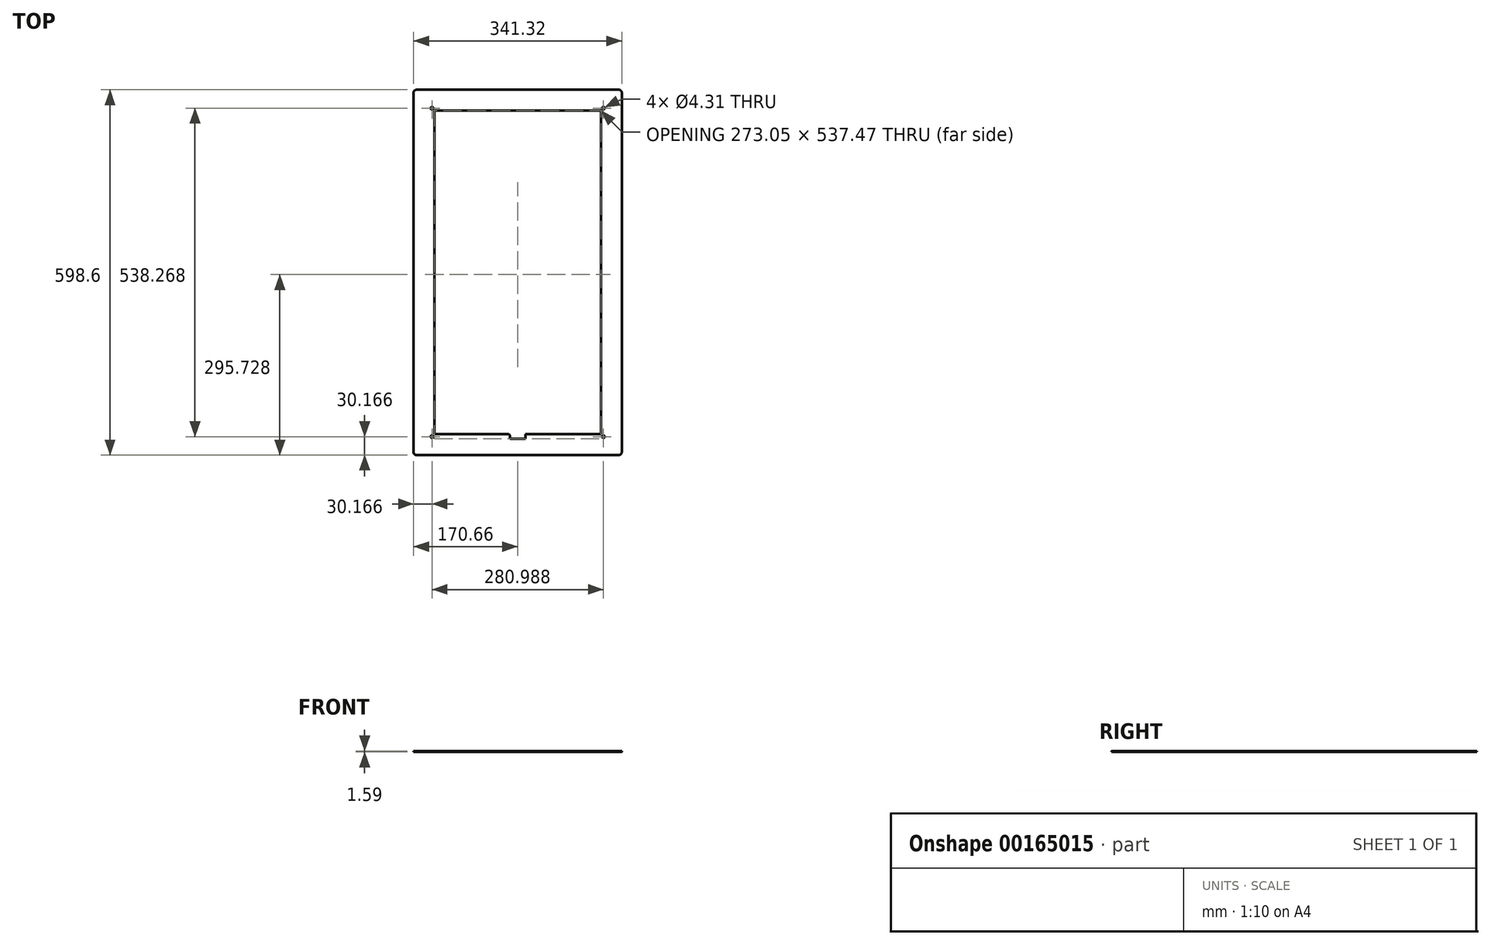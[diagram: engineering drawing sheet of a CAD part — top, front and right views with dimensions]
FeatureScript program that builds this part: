
annotation { "Feature Type Name" : "Feature", "Feature Type Description" : "" }
export const myFeature = defineFeature(function(context is Context, id is Id, definition is map)
    precondition{}
    {
        {
            var Q0;
            Q0=qCreatedBy(makeId("Top.planeOp"),FACE);
            var sketch = newSketch(context, id + "F0", { "sketchPlane" : qUnion([Q0])});
            skLineSegment(sketch, "E0.bottom", {"start": v(170.66, -299.3) * mm, "end": v(-170.66, -299.3) * mm});
            skLineSegment(sketch, "E0.top", {"start": v(170.66, 299.3) * mm, "end": v(-170.66, 299.3) * mm});
            skLineSegment(sketch, "E0.left", {"start": v(170.66, -299.3) * mm, "end": v(170.66, 299.3) * mm});
            skLineSegment(sketch, "E0.right", {"start": v(-170.66, -299.3) * mm, "end": v(-170.66, 299.3) * mm});
            skPoint(sketch, "E0.middle", {"position": v(0, 0) * mm});
            skLineSegment(sketch, "E1.bottom", {"start": v(140.5, 269.13) * mm, "end": v(-140.5, 269.13) * mm, "construction": true});
            skLineSegment(sketch, "E1.top", {"start": v(140.5, -269.13) * mm, "end": v(-140.5, -269.13) * mm, "construction": true});
            skLineSegment(sketch, "E1.left", {"start": v(140.5, 269.13) * mm, "end": v(140.5, -269.13) * mm, "construction": true});
            skLineSegment(sketch, "E1.right", {"start": v(-140.5, 269.13) * mm, "end": v(-140.5, -269.13) * mm, "construction": true});
            skLineSegment(sketch, "E2.bottom", {"start": v(136.53, 265.17) * mm, "end": v(-136.53, 265.17) * mm});
            skLineSegment(sketch, "E2.top", {"start": v(136.53, -265.17) * mm, "end": v(-136.53, -265.17) * mm});
            skLineSegment(sketch, "E2.left", {"start": v(136.53, 265.17) * mm, "end": v(136.53, -265.17) * mm});
            skLineSegment(sketch, "E2.right", {"start": v(-136.53, 265.17) * mm, "end": v(-136.53, -265.17) * mm});
            skLineSegment(sketch, "E3", {"start": v(136.53, 265.17) * mm, "end": v(136.53, 269.13) * mm, "construction": true});
            skLineSegment(sketch, "E4", {"start": v(136.53, 265.17) * mm, "end": v(140.5, 265.17) * mm, "construction": true});
            skLineSegment(sketch, "E5", {"start": v(140.5, 269.13) * mm, "end": v(140.5, 299.3) * mm, "construction": true});
            skLineSegment(sketch, "E6", {"start": v(140.5, 269.13) * mm, "end": v(170.66, 269.13) * mm, "construction": true});
            skCircle(sketch, "E7", {"center": v(-140.5, 269.13) * mm, "radius": 2.15 * mm});
            skCircle(sketch, "E8", {"center": v(140.5, 269.13) * mm, "radius": 2.15 * mm});
            skCircle(sketch, "E9", {"center": v(140.5, -269.13) * mm, "radius": 2.15 * mm});
            skCircle(sketch, "E10", {"center": v(-140.5, -269.13) * mm, "radius": 2.15 * mm});
            skSolve(sketch);
        }
        {
            var Q0;
            Q0=qSketchRegion(id+"F0",true);
            extrude(context, id + "F1", {"entities" : qUnion([Q0]), "depth" : 1.59 * mm});
        }
        {
            var Q0;
            Q0=makeQuery(id+"F1.opExtrude","SWEPT_EDGE",EDGE,{"disambiguationData":[OSD([sQuery(id+"F0.wireOp",EDGE,"E0.top"),sQuery(id+"F0.wireOp",EDGE,"E0.right")])]});
            var Q1;
            Q1=makeQuery(id+"F1.opExtrude","SWEPT_EDGE",EDGE,{"disambiguationData":[OSD([sQuery(id+"F0.wireOp",EDGE,"E0.top"),sQuery(id+"F0.wireOp",EDGE,"E0.left")])]});
            var Q2;
            Q2=makeQuery(id+"F1.opExtrude","SWEPT_EDGE",EDGE,{"disambiguationData":[OSD([sQuery(id+"F0.wireOp",EDGE,"E0.bottom"),sQuery(id+"F0.wireOp",EDGE,"E0.left")])]});
            var Q3;
            Q3=makeQuery(id+"F1.opExtrude","SWEPT_EDGE",EDGE,{"disambiguationData":[OSD([sQuery(id+"F0.wireOp",EDGE,"E0.bottom"),sQuery(id+"F0.wireOp",EDGE,"E0.right")])]});
            fillet(context, id + "F2", {"entities" : qUnion([Q0, Q1, Q2, Q3]), "radius" : 4.76 * mm, "tangentPropagation" : true, "allowEdgeOverflow" : false});
        }
        {
            var Q0;
            Q0=makeQuery(id+"F1.opExtrude","CAP_FACE",FACE,{"disambiguationData":[OSD([sQuery(id+"F0.wireOp",EDGE,"E0.bottom"),sQuery(id+"F0.wireOp",EDGE,"E0.top"),sQuery(id+"F0.wireOp",EDGE,"E0.left"),sQuery(id+"F0.wireOp",EDGE,"E0.right"),sQuery(id+"F0.wireOp",EDGE,"E2.bottom"),sQuery(id+"F0.wireOp",EDGE,"E2.top"),sQuery(id+"F0.wireOp",EDGE,"E2.left"),sQuery(id+"F0.wireOp",EDGE,"E2.right"),sQuery(id+"F0.wireOp",EDGE,"E7"),sQuery(id+"F0.wireOp",EDGE,"E8"),sQuery(id+"F0.wireOp",EDGE,"E9"),sQuery(id+"F0.wireOp",EDGE,"E10")])],"isStart":false});
            var sketch = newSketch(context, id + "F3", { "sketchPlane" : qUnion([Q0])});
            skLineSegment(sketch, "E11", {"start": v(-140.5, -269.13) * mm, "end": v(-140.5, -273.9) * mm, "construction": true});
            skLineSegment(sketch, "E12", {"start": v(-140.5, -273.9) * mm, "end": v(0, -273.9) * mm, "construction": true});
            skLineSegment(sketch, "E13", {"start": v(0, -273.9) * mm, "end": v(0, -272.3) * mm, "construction": true});
            skLineSegment(sketch, "E14.bottom", {"start": v(-12.7, -265.17) * mm, "end": v(12.7, -265.17) * mm});
            skLineSegment(sketch, "E14.top", {"start": v(-12.7, -272.3) * mm, "end": v(12.7, -272.3) * mm});
            skLineSegment(sketch, "E14.left", {"start": v(-12.7, -265.17) * mm, "end": v(-12.7, -272.3) * mm});
            skLineSegment(sketch, "E14.right", {"start": v(12.7, -265.17) * mm, "end": v(12.7, -272.3) * mm});
            skLineSegment(sketch, "E15", {"start": v(0, -273.9) * mm, "end": v(0, -299.3) * mm, "construction": true});
            skSolve(sketch);
        }
        {
            var Q0;
            Q0=qSketchRegion(id+"F3",true);
            var Q1;
            Q1=makeQuery(id+"F1.opExtrude","CAP_FACE",FACE,{"disambiguationData":[OSD([sQuery(id+"F0.wireOp",EDGE,"E0.bottom"),sQuery(id+"F0.wireOp",EDGE,"E0.top"),sQuery(id+"F0.wireOp",EDGE,"E0.left"),sQuery(id+"F0.wireOp",EDGE,"E0.right"),sQuery(id+"F0.wireOp",EDGE,"E2.bottom"),sQuery(id+"F0.wireOp",EDGE,"E2.top"),sQuery(id+"F0.wireOp",EDGE,"E2.left"),sQuery(id+"F0.wireOp",EDGE,"E2.right"),sQuery(id+"F0.wireOp",EDGE,"E7"),sQuery(id+"F0.wireOp",EDGE,"E8"),sQuery(id+"F0.wireOp",EDGE,"E9"),sQuery(id+"F0.wireOp",EDGE,"E10")])],"isStart":true});
            extrude(context, id + "F4", {"entities" : qUnion([Q0]), "operationType" : NewBodyOperationType.REMOVE, "endBound" : BoundingType.UP_TO_SURFACE, "oppositeDirection" : true, "endBoundEntityFace" : qUnion([Q1]), "depth" : 25.4 * mm});
        }
        {
            var Q0;
            Q0=makeQuery(id+"F4.boolean.opBoolean","COPY",EDGE,{"derivedFrom":makeQuery(id+"F4.opExtrude","SWEPT_EDGE",EDGE,{"disambiguationData":[OSD([sQuery(id+"F0.wireOp",EDGE,"E2.top"),sQuery(id+"F3.wireOp",EDGE,"E14.bottom"),sQuery(id+"F3.wireOp",EDGE,"E14.right")])]})});
            var Q1;
            Q1=makeQuery(id+"F4.boolean.opBoolean","COPY",EDGE,{"derivedFrom":makeQuery(id+"F4.opExtrude","SWEPT_EDGE",EDGE,{"disambiguationData":[OSD([sQuery(id+"F0.wireOp",EDGE,"E2.top"),sQuery(id+"F3.wireOp",EDGE,"E14.bottom"),sQuery(id+"F3.wireOp",EDGE,"E14.left")])]})});
            chamfer(context, id + "F5", {"entities" : qUnion([Q0, Q1]), "width" : 1.59 * mm, "tangentPropagation" : true});
        }
    });
